AUTODESK INVENTOR PART (.ipt)
format: ipt  version: 2019 (Build 230136000, 136)  size: 265,216 bytes
history: native  units: mm (DEFAULTED — no unit token found)
features: extrude x3, sketch x2, fillet x2, projected_geometry x2
ambient origin geometry x8: Origin, YZ Plane, XZ Plane, XY Plane, X Axis, Y Axis, Z Axis, Center Point
bodies: Body1 (feature_tree)
feature tree (9):
  sketch  "Sketch1"  dims[d2=5.5mm d3=6.5mm d4=8.0mm]
  extrude  "Extrusion2"  Depth=6.5mm
  fillet  "Fillet2"  Radius=8.0mm
  extrude  "Extrusion3"  Depth=1.5mm
  extrude  "Extrusion4"  Depth=4.0mm
  fillet  "Fillet3"  Radius=4.0mm
  sketch  "Sketch2"  dims[d5=13.5mm d9=1.5mm d10=4.0mm d11=4.0mm d12=1.5mm d13=6.0mm d14=0.0mm d15=0.5mm d16=12.5mm d17=0.0mm d18=3.5mm d19=3.5mm d20=4.0mm d21=0.0mm d22=0.5mm]
  projected_geometry  "Projected Loop1"
  projected_geometry  "Projected Loop2"
